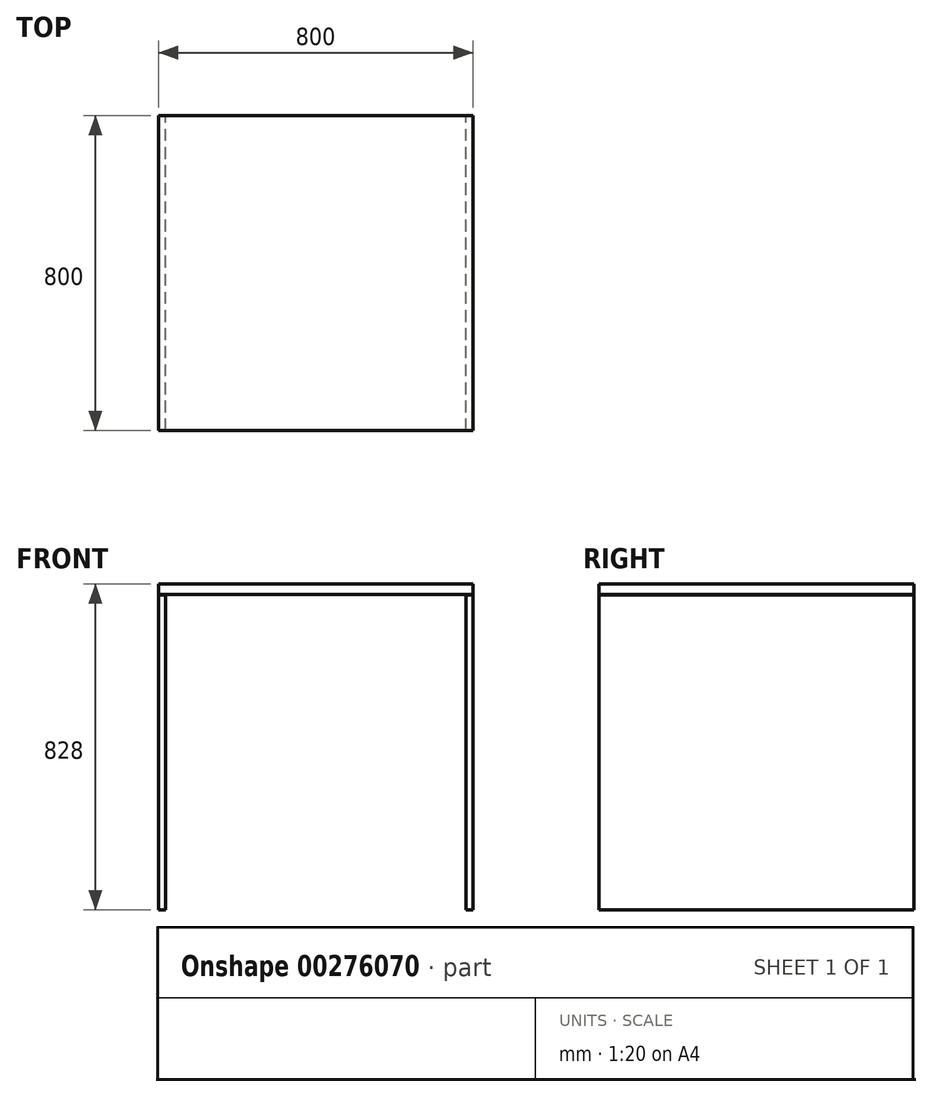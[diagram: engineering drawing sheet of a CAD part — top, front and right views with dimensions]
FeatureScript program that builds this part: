
annotation { "Feature Type Name" : "Feature", "Feature Type Description" : "" }
export const myFeature = defineFeature(function(context is Context, id is Id, definition is map)
    precondition{}
    {
        {
            var Q0;
            Q0=qCreatedBy(makeId("Front.planeOp"),FACE);
            var sketch = newSketch(context, id + "F0", { "sketchPlane" : qUnion([Q0])});
            skLineSegment(sketch, "E0.bottom", {"start": v(-400, 800) * mm, "end": v(-382, 800) * mm});
            skLineSegment(sketch, "E0.top", {"start": v(-400, 0) * mm, "end": v(-382, 0) * mm});
            skLineSegment(sketch, "E0.left", {"start": v(-400, 0) * mm, "end": v(-400, 800) * mm});
            skLineSegment(sketch, "E0.right", {"start": v(-382, 0) * mm, "end": v(-382, 800) * mm});
            skLineSegment(sketch, "E1.bottom", {"start": v(-400, 801) * mm, "end": v(400, 801) * mm});
            skLineSegment(sketch, "E1.top", {"start": v(-400, 828) * mm, "end": v(400, 828) * mm});
            skLineSegment(sketch, "E1.left", {"start": v(-400, 801) * mm, "end": v(-400, 828) * mm});
            skLineSegment(sketch, "E1.right", {"start": v(400, 801) * mm, "end": v(400, 828) * mm});
            skLineSegment(sketch, "E2.bottom", {"start": v(382, 0) * mm, "end": v(400, 0) * mm});
            skLineSegment(sketch, "E2.top", {"start": v(382, 800) * mm, "end": v(400, 800) * mm});
            skLineSegment(sketch, "E2.left", {"start": v(382, 0) * mm, "end": v(382, 800) * mm});
            skLineSegment(sketch, "E2.right", {"start": v(400, 0) * mm, "end": v(400, 800) * mm});
            skSolve(sketch);
        }
        {
            var Q0;
            Q0=makeQuery(id+"F0.imprint","IMPRINT",FACE,{"disambiguationData":[TD([[makeQuery(id+"F0.imprint","IMPRINT",EDGE,{"derivedFrom":sQuery(id+"F0.wireOp",EDGE,"E0.bottom")}),-1.0]])]});
            var Q1;
            Q1=makeQuery(id+"F0.imprint","IMPRINT",FACE,{"disambiguationData":[TD([[makeQuery(id+"F0.imprint","IMPRINT",EDGE,{"derivedFrom":sQuery(id+"F0.wireOp",EDGE,"E1.bottom")}),1.0]])]});
            var Q2;
            Q2=makeQuery(id+"F0.imprint","IMPRINT",FACE,{"disambiguationData":[TD([[makeQuery(id+"F0.imprint","IMPRINT",EDGE,{"derivedFrom":sQuery(id+"F0.wireOp",EDGE,"E2.bottom")}),1.0]])]});
            extrude(context, id + "F1", {"entities" : qUnion([Q0, Q1, Q2]), "depth" : 800 * mm});
        }
    });
